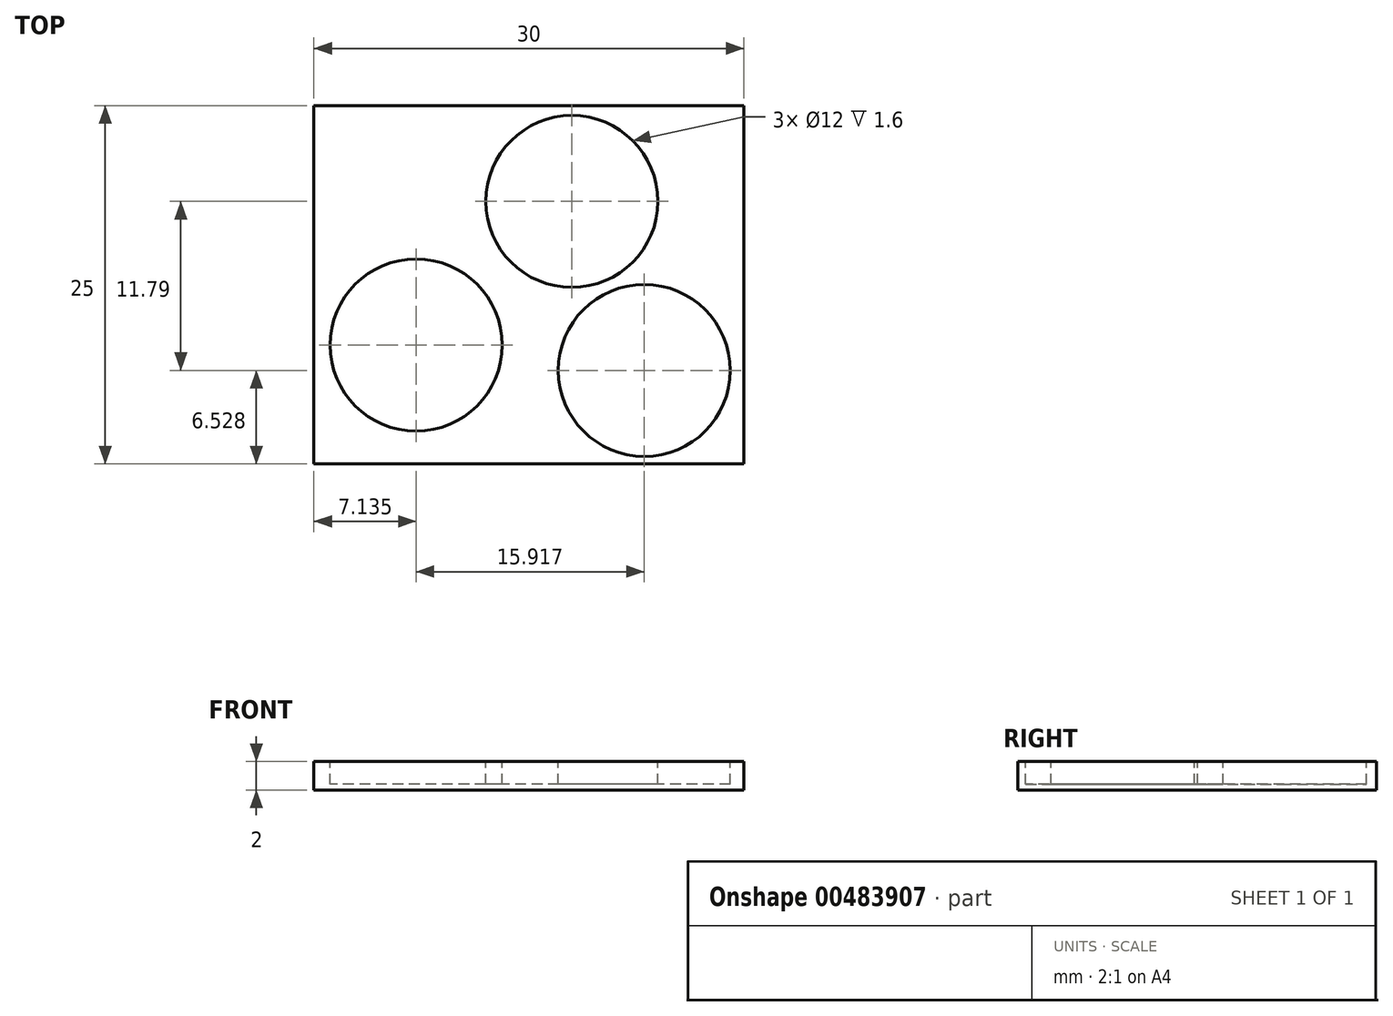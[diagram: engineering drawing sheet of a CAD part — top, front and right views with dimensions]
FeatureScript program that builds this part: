
annotation { "Feature Type Name" : "Feature", "Feature Type Description" : "" }
export const myFeature = defineFeature(function(context is Context, id is Id, definition is map)
    precondition{}
    {
        {
            var Q0;
            Q0=qCreatedBy(makeId("Top.planeOp"),FACE);
            var sketch = newSketch(context, id + "F0", { "sketchPlane" : qUnion([Q0])});
            skLineSegment(sketch, "E0.bottom", {"start": v(-15, 12.5) * mm, "end": v(15, 12.5) * mm});
            skLineSegment(sketch, "E0.top", {"start": v(-15, -12.5) * mm, "end": v(15, -12.5) * mm});
            skLineSegment(sketch, "E0.left", {"start": v(-15, 12.5) * mm, "end": v(-15, -12.5) * mm});
            skLineSegment(sketch, "E0.right", {"start": v(15, 12.5) * mm, "end": v(15, -12.5) * mm});
            skPoint(sketch, "E0.middle", {"position": v(0, 0) * mm});
            skSolve(sketch);
        }
        {
            var Q0;
            Q0=qSketchRegion(id+"F0",true);
            extrude(context, id + "F1", {"entities" : qUnion([Q0]), "oppositeDirection" : true, "depth" : 2 * mm});
        }
        {
            var Q0;
            Q0=qCreatedBy(makeId("Top.planeOp"),FACE);
            var sketch = newSketch(context, id + "F2", { "sketchPlane" : qUnion([Q0])});
            skCircle(sketch, "E1", {"center": v(-7.87, -4.2) * mm, "radius": 6 * mm});
            skCircle(sketch, "E2", {"center": v(3, 5.82) * mm, "radius": 6 * mm});
            skCircle(sketch, "E3", {"center": v(8.05, -5.97) * mm, "radius": 6 * mm});
            skSolve(sketch);
        }
        {
            var Q0;
            Q0=qSketchRegion(id+"F2",true);
            extrude(context, id + "F3", {"entities" : qUnion([Q0]), "operationType" : NewBodyOperationType.REMOVE, "oppositeDirection" : true, "offsetDistance" : 25 * mm, "depth" : 1.6 * mm});
        }
    });
